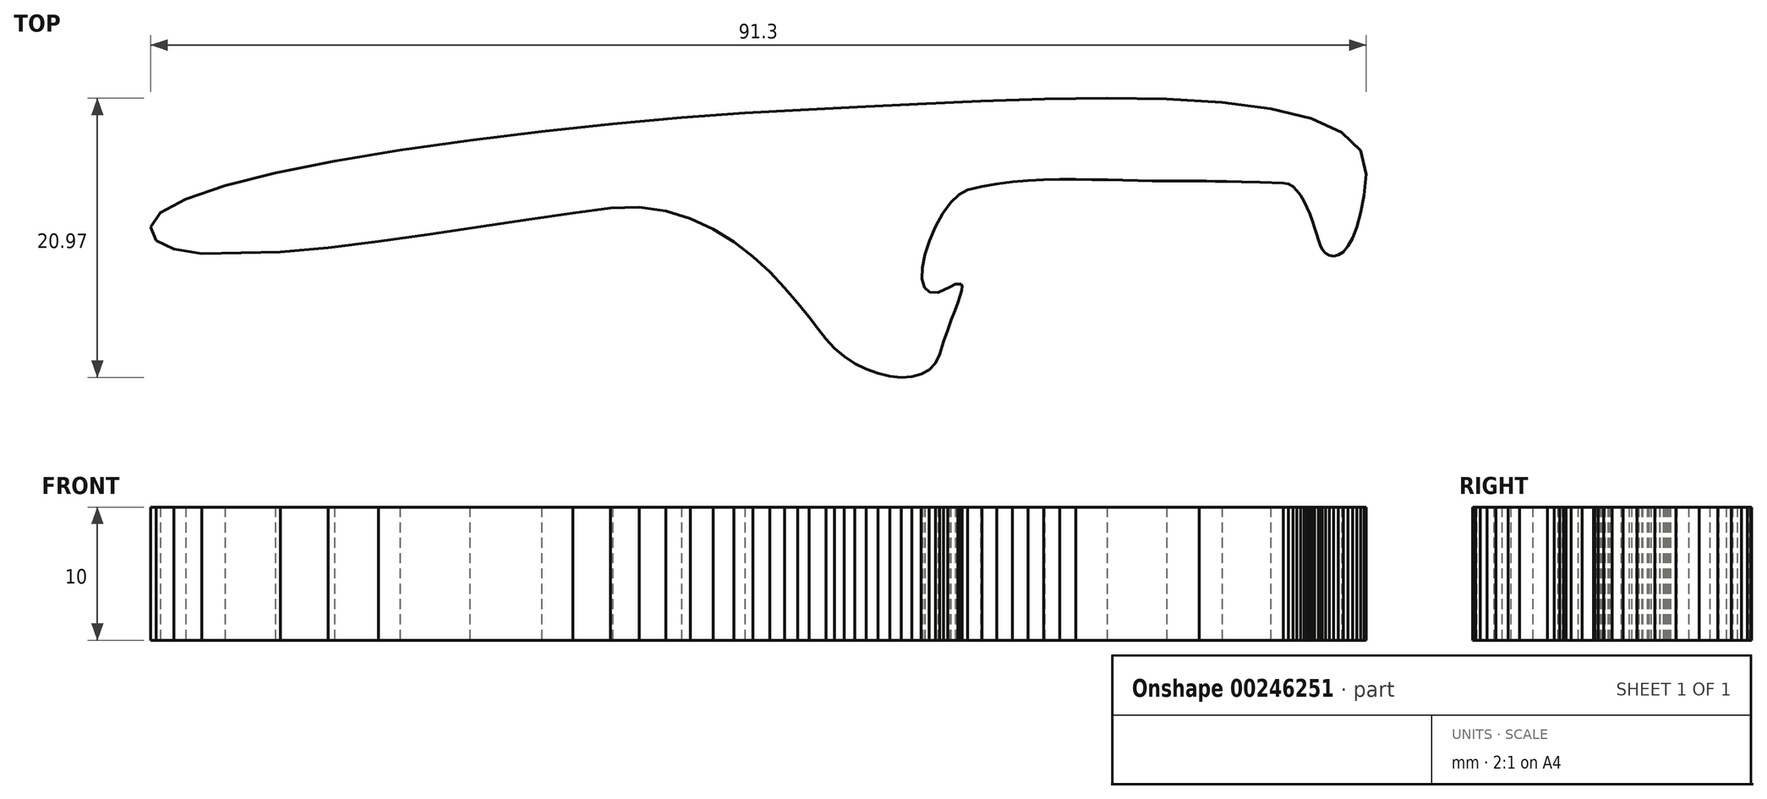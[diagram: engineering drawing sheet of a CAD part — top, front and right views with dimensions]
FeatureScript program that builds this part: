
annotation { "Feature Type Name" : "Feature", "Feature Type Description" : "" }
export const myFeature = defineFeature(function(context is Context, id is Id, definition is map)
    precondition{}
    {
        {
            var Q0;
            Q0=qCreatedBy(makeId("Top.planeOp"),FACE);
            var sketch = newSketch(context, id + "F0", { "sketchPlane" : qUnion([Q0])});
            skPoint(sketch, "E0.0", {"position": v(3.84, 7.67) * mm});
            skPoint(sketch, "E1.0", {"position": v(5.02, 7.76) * mm});
            skPoint(sketch, "E2.0", {"position": v(6.21, 7.83) * mm});
            skPoint(sketch, "E3.0", {"position": v(7.42, 7.85) * mm});
            skPoint(sketch, "E4.0", {"position": v(8.62, 7.86) * mm});
            skPoint(sketch, "E5.0", {"position": v(9.82, 7.84) * mm});
            skPoint(sketch, "E6.0", {"position": v(11, 7.82) * mm});
            skPoint(sketch, "E7.0", {"position": v(12.15, 7.78) * mm});
            skPoint(sketch, "E8.0", {"position": v(13.27, 7.76) * mm});
            skPoint(sketch, "E9.0", {"position": v(14.35, 7.74) * mm});
            skPoint(sketch, "E10.0", {"position": v(15.25, 7.73) * mm});
            skPoint(sketch, "E11.0", {"position": v(15.95, 7.73) * mm});
            skPoint(sketch, "E12.0", {"position": v(16.51, 7.73) * mm});
            skPoint(sketch, "E13.0", {"position": v(16.98, 7.73) * mm});
            skPoint(sketch, "E14.0", {"position": v(17.88, 7.73) * mm});
            skPoint(sketch, "E15.0", {"position": v(18.41, 7.73) * mm});
            skPoint(sketch, "E16.0", {"position": v(19.08, 7.72) * mm});
            skPoint(sketch, "E17.0", {"position": v(19.94, 7.7) * mm});
            skPoint(sketch, "E18.0", {"position": v(21.05, 7.67) * mm});
            skPoint(sketch, "E19.0", {"position": v(22.45, 7.63) * mm});
            skPoint(sketch, "E20.0", {"position": v(24.22, 7.57) * mm});
            skPoint(sketch, "E21.0", {"position": v(24.59, 7.5) * mm});
            skPoint(sketch, "E22.0", {"position": v(24.93, 7.3) * mm});
            skPoint(sketch, "E23.0", {"position": v(25.23, 7.02) * mm});
            skPoint(sketch, "E24.0", {"position": v(25.51, 6.65) * mm});
            skPoint(sketch, "E25.0", {"position": v(25.77, 6.22) * mm});
            skPoint(sketch, "E26.0", {"position": v(26, 5.75) * mm});
            skPoint(sketch, "E27.0", {"position": v(26.2, 5.24) * mm});
            skPoint(sketch, "E28.0", {"position": v(26.38, 4.73) * mm});
            skPoint(sketch, "E29.0", {"position": v(26.55, 4.23) * mm});
            skPoint(sketch, "E30.0", {"position": v(26.7, 3.75) * mm});
            skPoint(sketch, "E31.0", {"position": v(26.84, 3.3) * mm});
            skPoint(sketch, "E32.0", {"position": v(26.96, 2.93) * mm});
            skPoint(sketch, "E33.0", {"position": v(27.13, 2.58) * mm});
            skPoint(sketch, "E34.0", {"position": v(27.37, 2.3) * mm});
            skPoint(sketch, "E35.0", {"position": v(27.66, 2.14) * mm});
            skPoint(sketch, "E36.0", {"position": v(27.98, 2.08) * mm});
            skPoint(sketch, "E37.0", {"position": v(28.33, 2.17) * mm});
            skPoint(sketch, "E38.0", {"position": v(28.7, 2.41) * mm});
            skPoint(sketch, "E39.0", {"position": v(29.06, 2.83) * mm});
            skPoint(sketch, "E40.0", {"position": v(29.41, 3.45) * mm});
            skPoint(sketch, "E41.0", {"position": v(29.73, 4.28) * mm});
            skPoint(sketch, "E42.0", {"position": v(30.02, 5.34) * mm});
            skPoint(sketch, "E43.0", {"position": v(30.25, 6.66) * mm});
            skPoint(sketch, "E44.0", {"position": v(30.42, 8.25) * mm});
            skPoint(sketch, "E45.0", {"position": v(30.02, 10.02) * mm});
            skPoint(sketch, "E46.0", {"position": v(28.6, 11.4) * mm});
            skPoint(sketch, "E47.0", {"position": v(26.3, 12.43) * mm});
            skPoint(sketch, "E48.0", {"position": v(23.25, 13.16) * mm});
            skPoint(sketch, "E49.0", {"position": v(19.6, 13.63) * mm});
            skPoint(sketch, "E50.0", {"position": v(15.45, 13.88) * mm});
            skPoint(sketch, "E51.0", {"position": v(10.96, 13.95) * mm});
            skPoint(sketch, "E52.0", {"position": v(6.25, 13.89) * mm});
            skPoint(sketch, "E53.0", {"position": v(1.47, 13.73) * mm});
            skPoint(sketch, "E54.0", {"position": v(-16.25, 12.85) * mm});
            skPoint(sketch, "E55.0", {"position": v(-12.04, 13.08) * mm});
            skPoint(sketch, "E56.0", {"position": v(-7.81, 13.28) * mm});
            skPoint(sketch, "E57.0", {"position": v(-3.27, 13.5) * mm});
            skPoint(sketch, "E58.0", {"position": v(-21.02, 12.5) * mm});
            skPoint(sketch, "E59.0", {"position": v(-26.17, 12.04) * mm});
            skPoint(sketch, "E60.0", {"position": v(-31.53, 11.46) * mm});
            skPoint(sketch, "E61.0", {"position": v(-36.91, 10.8) * mm});
            skPoint(sketch, "E62.0", {"position": v(-42.16, 10.05) * mm});
            skPoint(sketch, "E63.0", {"position": v(-47.1, 9.22) * mm});
            skPoint(sketch, "E64.0", {"position": v(-51.53, 8.33) * mm});
            skPoint(sketch, "E65.0", {"position": v(-55.3, 7.38) * mm});
            skPoint(sketch, "E66.0", {"position": v(-58.23, 6.38) * mm});
            skPoint(sketch, "E67.0", {"position": v(-60.15, 5.34) * mm});
            skPoint(sketch, "E68.0", {"position": v(-60.88, 4.27) * mm});
            skPoint(sketch, "E69.0", {"position": v(-60.47, 3.26) * mm});
            skPoint(sketch, "E70.0", {"position": v(-59.15, 2.6) * mm});
            skPoint(sketch, "E71.0", {"position": v(-57.06, 2.28) * mm});
            skPoint(sketch, "E72.0", {"position": v(-51.13, 2.39) * mm});
            skPoint(sketch, "E73.0", {"position": v(-47.56, 2.73) * mm});
            skPoint(sketch, "E74.0", {"position": v(-43.78, 3.2) * mm});
            skPoint(sketch, "E75.0", {"position": v(-39.9, 3.73) * mm});
            skPoint(sketch, "E76.0", {"position": v(-36.09, 4.3) * mm});
            skPoint(sketch, "E77.0", {"position": v(-32.46, 4.85) * mm});
            skPoint(sketch, "E78.0", {"position": v(-29.16, 5.33) * mm});
            skPoint(sketch, "E79.0", {"position": v(-26.33, 5.7) * mm});
            skPoint(sketch, "E80.0", {"position": v(-22.2, 5.48) * mm});
            skPoint(sketch, "E81.0", {"position": v(-20.34, 4.92) * mm});
            skPoint(sketch, "E82.0", {"position": v(-18.64, 4.13) * mm});
            skPoint(sketch, "E83.0", {"position": v(-17.07, 3.16) * mm});
            skPoint(sketch, "E84.0", {"position": v(-24.2, 5.75) * mm});
            skPoint(sketch, "E85.0", {"position": v(-15.66, 2.06) * mm});
            skPoint(sketch, "E86.0", {"position": v(-14.38, 0.9) * mm});
            skPoint(sketch, "E87.0", {"position": v(-13.25, -0.29) * mm});
            skPoint(sketch, "E88.0", {"position": v(-12.26, -1.43) * mm});
            skPoint(sketch, "E89.0", {"position": v(-11.42, -2.5) * mm});
            skPoint(sketch, "E90.0", {"position": v(-10.72, -3.42) * mm});
            skPoint(sketch, "E91.0", {"position": v(-10.16, -4.14) * mm});
            skPoint(sketch, "E92.0", {"position": v(74.69, 13.96) * mm});
            skPoint(sketch, "E93.0", {"position": v(-9.52, -4.83) * mm});
            skPoint(sketch, "E94.0", {"position": v(-8.79, -5.44) * mm});
            skPoint(sketch, "E95.0", {"position": v(-7.12, -6.4) * mm});
            skPoint(sketch, "E96.0", {"position": v(-7.98, -5.96) * mm});
            skPoint(sketch, "E97.0", {"position": v(-6.24, -6.72) * mm});
            skPoint(sketch, "E98.0", {"position": v(-5.36, -6.93) * mm});
            skPoint(sketch, "E99.0", {"position": v(-4.51, -7.02) * mm});
            skPoint(sketch, "E100.0", {"position": v(-3.72, -6.97) * mm});
            skPoint(sketch, "E101.0", {"position": v(-3, -6.79) * mm});
            skPoint(sketch, "E102.0", {"position": v(-2.4, -6.44) * mm});
            skPoint(sketch, "E103.0", {"position": v(-1.92, -5.94) * mm});
            skPoint(sketch, "E104.0", {"position": v(-1.6, -5.27) * mm});
            skPoint(sketch, "E105.0", {"position": v(-1.32, -4.34) * mm});
            skPoint(sketch, "E106.0", {"position": v(-1.02, -3.49) * mm});
            skPoint(sketch, "E107.0", {"position": v(-0.74, -2.7) * mm});
            skPoint(sketch, "E108.0", {"position": v(-0.48, -2) * mm});
            skPoint(sketch, "E109.0", {"position": v(-0.26, -1.4) * mm});
            skPoint(sketch, "E110.0", {"position": v(-0.08, -0.89) * mm});
            skPoint(sketch, "E111.0", {"position": v(0.03, -0.48) * mm});
            skPoint(sketch, "E112.0", {"position": v(0.06, -0.18) * mm});
            skPoint(sketch, "E113.0", {"position": v(0, 0) * mm});
            skPoint(sketch, "E114.0", {"position": v(-0.44, -0.02) * mm});
            skPoint(sketch, "E115.0", {"position": v(-0.85, -0.24) * mm});
            skPoint(sketch, "E116.0", {"position": v(-1.75, -0.64) * mm});
            skPoint(sketch, "E117.0", {"position": v(-2.38, -0.63) * mm});
            skPoint(sketch, "E118.0", {"position": v(-2.76, -0.27) * mm});
            skPoint(sketch, "E119.0", {"position": v(-2.93, 0.37) * mm});
            skPoint(sketch, "E120.0", {"position": v(-2.9, 1.22) * mm});
            skPoint(sketch, "E121.0", {"position": v(-2.7, 2.2) * mm});
            skPoint(sketch, "E122.0", {"position": v(-2.37, 3.25) * mm});
            skPoint(sketch, "E123.0", {"position": v(-1.92, 4.3) * mm});
            skPoint(sketch, "E124.0", {"position": v(-1.39, 5.28) * mm});
            skPoint(sketch, "E125.0", {"position": v(-0.8, 6.1) * mm});
            skPoint(sketch, "E126.0", {"position": v(-0.16, 6.73) * mm});
            skPoint(sketch, "E127.0", {"position": v(0.47, 7.07) * mm});
            skPoint(sketch, "E128.0", {"position": v(1.56, 7.32) * mm});
            skPoint(sketch, "E129.0", {"position": v(2.68, 7.52) * mm});
            skLineSegment(sketch, "E130", {"start": v(-58.23, 6.38) * mm, "end": v(-55.3, 7.38) * mm});
            skLineSegment(sketch, "E131", {"start": v(-51.53, 8.33) * mm, "end": v(-55.3, 7.38) * mm});
            skLineSegment(sketch, "E132", {"start": v(-51.53, 8.33) * mm, "end": v(-47.1, 9.22) * mm});
            skLineSegment(sketch, "E133", {"start": v(-47.1, 9.22) * mm, "end": v(-42.16, 10.05) * mm});
            skLineSegment(sketch, "E134", {"start": v(-42.16, 10.05) * mm, "end": v(-36.91, 10.8) * mm});
            skLineSegment(sketch, "E135", {"start": v(-36.91, 10.8) * mm, "end": v(-31.53, 11.46) * mm});
            skLineSegment(sketch, "E136", {"start": v(-31.53, 11.46) * mm, "end": v(-26.17, 12.04) * mm});
            skLineSegment(sketch, "E137", {"start": v(-26.17, 12.04) * mm, "end": v(-21.02, 12.5) * mm});
            skLineSegment(sketch, "E138", {"start": v(-21.02, 12.5) * mm, "end": v(-16.25, 12.85) * mm});
            skLineSegment(sketch, "E139", {"start": v(-16.25, 12.85) * mm, "end": v(-12.04, 13.08) * mm});
            skLineSegment(sketch, "E140", {"start": v(-12.04, 13.08) * mm, "end": v(-7.81, 13.28) * mm});
            skLineSegment(sketch, "E141", {"start": v(-7.81, 13.28) * mm, "end": v(-3.27, 13.5) * mm});
            skLineSegment(sketch, "E142", {"start": v(-3.27, 13.5) * mm, "end": v(1.47, 13.73) * mm});
            skLineSegment(sketch, "E143", {"start": v(1.47, 13.73) * mm, "end": v(6.25, 13.89) * mm});
            skLineSegment(sketch, "E144", {"start": v(6.25, 13.89) * mm, "end": v(10.96, 13.95) * mm});
            skLineSegment(sketch, "E145", {"start": v(10.96, 13.95) * mm, "end": v(15.45, 13.88) * mm});
            skLineSegment(sketch, "E146", {"start": v(15.45, 13.88) * mm, "end": v(19.6, 13.63) * mm});
            skLineSegment(sketch, "E147", {"start": v(19.6, 13.63) * mm, "end": v(23.25, 13.16) * mm});
            skLineSegment(sketch, "E148", {"start": v(26.3, 12.43) * mm, "end": v(23.25, 13.16) * mm});
            skLineSegment(sketch, "E149", {"start": v(26.3, 12.43) * mm, "end": v(28.6, 11.4) * mm});
            skLineSegment(sketch, "E150", {"start": v(28.6, 11.4) * mm, "end": v(30.02, 10.02) * mm});
            skLineSegment(sketch, "E151", {"start": v(30.02, 10.02) * mm, "end": v(30.42, 8.25) * mm});
            skLineSegment(sketch, "E152", {"start": v(30.42, 8.25) * mm, "end": v(30.25, 6.66) * mm});
            skLineSegment(sketch, "E153", {"start": v(30.25, 6.66) * mm, "end": v(30.02, 5.34) * mm});
            skLineSegment(sketch, "E154", {"start": v(30.02, 5.34) * mm, "end": v(29.73, 4.28) * mm});
            skLineSegment(sketch, "E155", {"start": v(29.73, 4.28) * mm, "end": v(29.41, 3.45) * mm});
            skLineSegment(sketch, "E156", {"start": v(29.41, 3.45) * mm, "end": v(29.06, 2.83) * mm});
            skLineSegment(sketch, "E157", {"start": v(29.06, 2.83) * mm, "end": v(28.7, 2.41) * mm});
            skLineSegment(sketch, "E158", {"start": v(28.7, 2.41) * mm, "end": v(28.33, 2.17) * mm});
            skLineSegment(sketch, "E159", {"start": v(28.33, 2.17) * mm, "end": v(27.98, 2.08) * mm});
            skLineSegment(sketch, "E160", {"start": v(27.98, 2.08) * mm, "end": v(27.66, 2.14) * mm});
            skLineSegment(sketch, "E161", {"start": v(27.66, 2.14) * mm, "end": v(27.37, 2.3) * mm});
            skLineSegment(sketch, "E162", {"start": v(27.37, 2.3) * mm, "end": v(27.13, 2.58) * mm});
            skLineSegment(sketch, "E163", {"start": v(27.13, 2.58) * mm, "end": v(26.96, 2.93) * mm});
            skLineSegment(sketch, "E164", {"start": v(26.96, 2.93) * mm, "end": v(26.84, 3.3) * mm});
            skLineSegment(sketch, "E165", {"start": v(26.84, 3.3) * mm, "end": v(26.7, 3.75) * mm});
            skLineSegment(sketch, "E166", {"start": v(26.7, 3.75) * mm, "end": v(26.55, 4.23) * mm});
            skLineSegment(sketch, "E167", {"start": v(26.55, 4.23) * mm, "end": v(26.38, 4.73) * mm});
            skLineSegment(sketch, "E168", {"start": v(26.38, 4.73) * mm, "end": v(26.2, 5.24) * mm});
            skLineSegment(sketch, "E169", {"start": v(26.2, 5.24) * mm, "end": v(26, 5.75) * mm});
            skLineSegment(sketch, "E170", {"start": v(26, 5.75) * mm, "end": v(25.77, 6.22) * mm});
            skLineSegment(sketch, "E171", {"start": v(25.77, 6.22) * mm, "end": v(25.51, 6.65) * mm});
            skLineSegment(sketch, "E172", {"start": v(25.23, 7.02) * mm, "end": v(25.51, 6.65) * mm});
            skLineSegment(sketch, "E173", {"start": v(24.93, 7.3) * mm, "end": v(25.23, 7.02) * mm});
            skLineSegment(sketch, "E174", {"start": v(24.59, 7.5) * mm, "end": v(24.93, 7.3) * mm});
            skLineSegment(sketch, "E175", {"start": v(24.22, 7.57) * mm, "end": v(24.59, 7.5) * mm});
            skLineSegment(sketch, "E176", {"start": v(22.45, 7.63) * mm, "end": v(24.22, 7.57) * mm});
            skLineSegment(sketch, "E177", {"start": v(21.05, 7.67) * mm, "end": v(22.45, 7.63) * mm});
            skLineSegment(sketch, "E178", {"start": v(19.94, 7.7) * mm, "end": v(21.05, 7.67) * mm});
            skLineSegment(sketch, "E179", {"start": v(19.08, 7.72) * mm, "end": v(19.94, 7.7) * mm});
            skLineSegment(sketch, "E180", {"start": v(18.41, 7.73) * mm, "end": v(19.08, 7.72) * mm});
            skLineSegment(sketch, "E181", {"start": v(17.88, 7.73) * mm, "end": v(18.41, 7.73) * mm});
            skLineSegment(sketch, "E182", {"start": v(16.98, 7.73) * mm, "end": v(17.88, 7.73) * mm});
            skLineSegment(sketch, "E183", {"start": v(16.51, 7.73) * mm, "end": v(16.98, 7.73) * mm});
            skLineSegment(sketch, "E184", {"start": v(16.51, 7.73) * mm, "end": v(15.95, 7.73) * mm});
            skLineSegment(sketch, "E185", {"start": v(15.95, 7.73) * mm, "end": v(15.25, 7.73) * mm});
            skLineSegment(sketch, "E186", {"start": v(15.25, 7.73) * mm, "end": v(14.35, 7.74) * mm});
            skLineSegment(sketch, "E187", {"start": v(14.35, 7.74) * mm, "end": v(13.27, 7.76) * mm});
            skLineSegment(sketch, "E188", {"start": v(13.27, 7.76) * mm, "end": v(12.15, 7.78) * mm});
            skLineSegment(sketch, "E189", {"start": v(12.15, 7.78) * mm, "end": v(11, 7.82) * mm});
            skLineSegment(sketch, "E190", {"start": v(-2.93, 0.37) * mm, "end": v(-2.76, -0.27) * mm});
            skLineSegment(sketch, "E191", {"start": v(-2.76, -0.27) * mm, "end": v(-2.38, -0.63) * mm});
            skLineSegment(sketch, "E192", {"start": v(-2.38, -0.63) * mm, "end": v(-1.75, -0.64) * mm});
            skLineSegment(sketch, "E193", {"start": v(-1.75, -0.64) * mm, "end": v(-0.85, -0.24) * mm});
            skLineSegment(sketch, "E194", {"start": v(-0.85, -0.24) * mm, "end": v(-0.44, -0.02) * mm});
            skLineSegment(sketch, "E195", {"start": v(-0.44, -0.02) * mm, "end": v(0, 0) * mm});
            skLineSegment(sketch, "E196", {"start": v(0, 0) * mm, "end": v(0.06, -0.18) * mm});
            skLineSegment(sketch, "E197", {"start": v(0.06, -0.18) * mm, "end": v(0.03, -0.48) * mm});
            skLineSegment(sketch, "E198", {"start": v(0.03, -0.48) * mm, "end": v(-0.08, -0.89) * mm});
            skLineSegment(sketch, "E199", {"start": v(-0.08, -0.89) * mm, "end": v(-0.26, -1.4) * mm});
            skLineSegment(sketch, "E200", {"start": v(-0.26, -1.4) * mm, "end": v(-0.48, -2) * mm});
            skLineSegment(sketch, "E201", {"start": v(-0.48, -2) * mm, "end": v(-0.74, -2.7) * mm});
            skLineSegment(sketch, "E202", {"start": v(-0.74, -2.7) * mm, "end": v(-1.02, -3.49) * mm});
            skLineSegment(sketch, "E203", {"start": v(-2.93, 0.37) * mm, "end": v(-2.9, 1.22) * mm});
            skLineSegment(sketch, "E204", {"start": v(-2.9, 1.22) * mm, "end": v(-2.7, 2.2) * mm});
            skLineSegment(sketch, "E205", {"start": v(-58.23, 6.38) * mm, "end": v(-60.15, 5.34) * mm});
            skLineSegment(sketch, "E206", {"start": v(-60.15, 5.34) * mm, "end": v(-60.88, 4.27) * mm});
            skLineSegment(sketch, "E207", {"start": v(-60.88, 4.27) * mm, "end": v(-60.47, 3.26) * mm});
            skLineSegment(sketch, "E208", {"start": v(-60.47, 3.26) * mm, "end": v(-59.15, 2.6) * mm});
            skLineSegment(sketch, "E209", {"start": v(-59.15, 2.6) * mm, "end": v(-57.06, 2.28) * mm});
            skLineSegment(sketch, "E210", {"start": v(-57.06, 2.28) * mm, "end": v(-51.13, 2.39) * mm});
            skLineSegment(sketch, "E211", {"start": v(-2.7, 2.2) * mm, "end": v(-2.37, 3.25) * mm});
            skLineSegment(sketch, "E212", {"start": v(-1.92, 4.3) * mm, "end": v(-2.37, 3.25) * mm});
            skLineSegment(sketch, "E213", {"start": v(-1.92, 4.3) * mm, "end": v(-1.39, 5.28) * mm});
            skLineSegment(sketch, "E214", {"start": v(-1.39, 5.28) * mm, "end": v(-0.8, 6.1) * mm});
            skLineSegment(sketch, "E215", {"start": v(-0.8, 6.1) * mm, "end": v(-0.16, 6.73) * mm});
            skLineSegment(sketch, "E216", {"start": v(-0.16, 6.73) * mm, "end": v(0.47, 7.07) * mm});
            skLineSegment(sketch, "E217", {"start": v(0.47, 7.07) * mm, "end": v(1.56, 7.32) * mm});
            skLineSegment(sketch, "E218", {"start": v(1.56, 7.32) * mm, "end": v(2.68, 7.52) * mm});
            skLineSegment(sketch, "E219", {"start": v(2.68, 7.52) * mm, "end": v(3.84, 7.67) * mm});
            skLineSegment(sketch, "E220", {"start": v(3.84, 7.67) * mm, "end": v(5.02, 7.76) * mm});
            skLineSegment(sketch, "E221", {"start": v(5.02, 7.76) * mm, "end": v(6.21, 7.83) * mm});
            skLineSegment(sketch, "E222", {"start": v(6.21, 7.83) * mm, "end": v(7.42, 7.85) * mm});
            skLineSegment(sketch, "E223", {"start": v(7.42, 7.85) * mm, "end": v(8.62, 7.86) * mm});
            skLineSegment(sketch, "E224", {"start": v(8.62, 7.86) * mm, "end": v(9.82, 7.84) * mm});
            skLineSegment(sketch, "E225", {"start": v(9.82, 7.84) * mm, "end": v(11, 7.82) * mm});
            skLineSegment(sketch, "E226", {"start": v(-1.02, -3.49) * mm, "end": v(-1.32, -4.34) * mm});
            skLineSegment(sketch, "E227", {"start": v(-1.32, -4.34) * mm, "end": v(-1.6, -5.27) * mm});
            skLineSegment(sketch, "E228", {"start": v(-1.6, -5.27) * mm, "end": v(-1.92, -5.94) * mm});
            skLineSegment(sketch, "E229", {"start": v(-1.92, -5.94) * mm, "end": v(-2.4, -6.44) * mm});
            skLineSegment(sketch, "E230", {"start": v(-2.4, -6.44) * mm, "end": v(-3, -6.79) * mm});
            skLineSegment(sketch, "E231", {"start": v(-3, -6.79) * mm, "end": v(-3.72, -6.97) * mm});
            skLineSegment(sketch, "E232", {"start": v(-3.72, -6.97) * mm, "end": v(-4.51, -7.02) * mm});
            skLineSegment(sketch, "E233", {"start": v(-4.51, -7.02) * mm, "end": v(-5.36, -6.93) * mm});
            skLineSegment(sketch, "E234", {"start": v(-6.24, -6.72) * mm, "end": v(-5.36, -6.93) * mm});
            skLineSegment(sketch, "E235", {"start": v(-7.12, -6.4) * mm, "end": v(-6.24, -6.72) * mm});
            skLineSegment(sketch, "E236", {"start": v(-7.98, -5.96) * mm, "end": v(-7.12, -6.4) * mm});
            skLineSegment(sketch, "E237", {"start": v(-8.79, -5.44) * mm, "end": v(-7.98, -5.96) * mm});
            skLineSegment(sketch, "E238", {"start": v(-9.52, -4.83) * mm, "end": v(-8.79, -5.44) * mm});
            skLineSegment(sketch, "E239", {"start": v(-10.16, -4.14) * mm, "end": v(-9.52, -4.83) * mm});
            skLineSegment(sketch, "E240", {"start": v(-10.72, -3.42) * mm, "end": v(-10.16, -4.14) * mm});
            skLineSegment(sketch, "E241", {"start": v(-11.42, -2.5) * mm, "end": v(-10.72, -3.42) * mm});
            skLineSegment(sketch, "E242", {"start": v(-12.26, -1.43) * mm, "end": v(-11.42, -2.5) * mm});
            skLineSegment(sketch, "E243", {"start": v(-13.25, -0.29) * mm, "end": v(-12.26, -1.43) * mm});
            skLineSegment(sketch, "E244", {"start": v(-14.38, 0.9) * mm, "end": v(-13.25, -0.29) * mm});
            skLineSegment(sketch, "E245", {"start": v(-15.66, 2.06) * mm, "end": v(-14.38, 0.9) * mm});
            skLineSegment(sketch, "E246", {"start": v(-17.07, 3.16) * mm, "end": v(-15.66, 2.06) * mm});
            skLineSegment(sketch, "E247", {"start": v(-18.64, 4.13) * mm, "end": v(-17.07, 3.16) * mm});
            skLineSegment(sketch, "E248", {"start": v(-20.34, 4.92) * mm, "end": v(-18.64, 4.13) * mm});
            skLineSegment(sketch, "E249", {"start": v(-22.2, 5.48) * mm, "end": v(-20.34, 4.92) * mm});
            skLineSegment(sketch, "E250", {"start": v(-24.2, 5.75) * mm, "end": v(-22.2, 5.48) * mm});
            skLineSegment(sketch, "E251", {"start": v(-26.33, 5.7) * mm, "end": v(-24.2, 5.75) * mm});
            skLineSegment(sketch, "E252", {"start": v(-29.16, 5.33) * mm, "end": v(-26.33, 5.7) * mm});
            skLineSegment(sketch, "E253", {"start": v(-32.46, 4.85) * mm, "end": v(-29.16, 5.33) * mm});
            skLineSegment(sketch, "E254", {"start": v(-36.09, 4.3) * mm, "end": v(-32.46, 4.85) * mm});
            skLineSegment(sketch, "E255", {"start": v(-39.9, 3.73) * mm, "end": v(-36.09, 4.3) * mm});
            skLineSegment(sketch, "E256", {"start": v(-43.78, 3.2) * mm, "end": v(-39.9, 3.73) * mm});
            skLineSegment(sketch, "E257", {"start": v(-47.56, 2.73) * mm, "end": v(-43.78, 3.2) * mm});
            skLineSegment(sketch, "E258", {"start": v(-51.13, 2.39) * mm, "end": v(-47.56, 2.73) * mm});
            skSolve(sketch);
        }
        {
            var Q0;
            Q0=makeQuery(id+"F0.imprint","IMPRINT",FACE,{"disambiguationData":[TD([[makeQuery(id+"F0.imprint","IMPRINT",EDGE,{"derivedFrom":sQuery(id+"F0.wireOp",EDGE,"E130")}),-1.0]])]});
            extrude(context, id + "F1", {"entities" : qUnion([Q0]), "depth" : 10 * mm, "offsetDistance" : 25 * mm});
        }
    });
